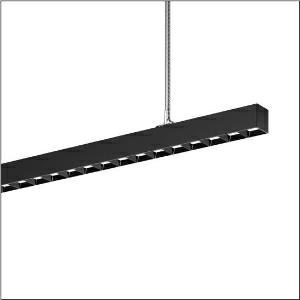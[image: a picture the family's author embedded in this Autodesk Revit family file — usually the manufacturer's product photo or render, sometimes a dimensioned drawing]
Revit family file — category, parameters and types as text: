
# Revit family: silica_r__21_51mx34dc3dbb_b9b0
name_source: partatom
category: Lighting Fixtures
units: mm (PartAtom-declared; Revit-internal decimal feet)

## family parameters
Cut with Voids When Loaded = No
Host = Face
Light Source = No
Part Type = Normal
Room Calculation Point = No
Round Connector Dimension = Use Diameter
Shared = No

## types (1)
- --- (1 x LED, 19200 lm, 129.1 W, 3000K)
    Apparent Load = 129 VA
    CIE Flux Codes = 74 94 99 56 100
    Color Rendering = 80
    Color Temperature = 3000K
    Default Elevation = 1800 mm
    Description = Silica® 21, office luminaire, primary light control with darklight reflector, of PMMA, black, light emission: direct/indirect distribution, primary light characteristic: asymmetric, installation type: suspended mounting, LED, rated luminous flux: 19.200lm, luminous efficacy: 149lm/W, light colour: 830, colour temperature: 3000K, with terminal, 3+2-pole, max. 2.5mm², mains connection: 220..240V, AC, 50/60Hz, rated input power: 129.1W, luminaire housing, of aluminium, jet black (RAL 9005), length: 3.004mm, width: 53mm, height: 53mm, protection rating (complete): IP20, insulation class (complete): insulation class I (protective earthing), certification: CE, permissible operating ambient temperature: 0..+35°C, standard: EN 50419, packaging unit: 1 piece
    Height = 53 mm
    Lamp = 1 x LED
    Lamp Light Flux = 19200 lm
    Lamp Power = 129.1 W
    Lamp count = 1
    Length = 3004 mm
    Luminous efficacy = 149 lm/W
    Manufacturer = Siteco
    ModVariant = No
    Model = 51MX34DC3DBB
    Mounting Place = Ceiling
    Mounting Type = Pendant
    Number of Poles = 1
    OnlyDefault = Yes
    Power Factor = 1
    Product Name = Silica® 21
    Product group = office luminaire | ceiling pendant
    ProductGroupID = 902
    Protection Class = Protection class I
    Protection Degree = IP 20
    RLX_Detail_Level = 1
    RLX_Emergency_Light_Flux = 0 lm
    RLX_Emergency_Type = 0
    RLX_Emergency_Type_DB = No
    RlxData = <blob elided: 67605 chars, md5=932e1f09>
    Socket = socket
    Standby Power = 0 W
    System Light Flux = 19200 lm
    System Power = 129 W
    Type Comments = factory setting: luminous flux: 100 % | dim-lin: 254 | 448 mA
    Type Image = l_1335852.jpg
    URL = http://relux.com
    VarID = @adj_089555
    Voltage = 0 V
    Weight = 0.00 kg
    Width = 53 mm

## geometry (parser evidence)
native form markers: Blend x4, Sweep x12
no freeform markers — native parametric forms only
